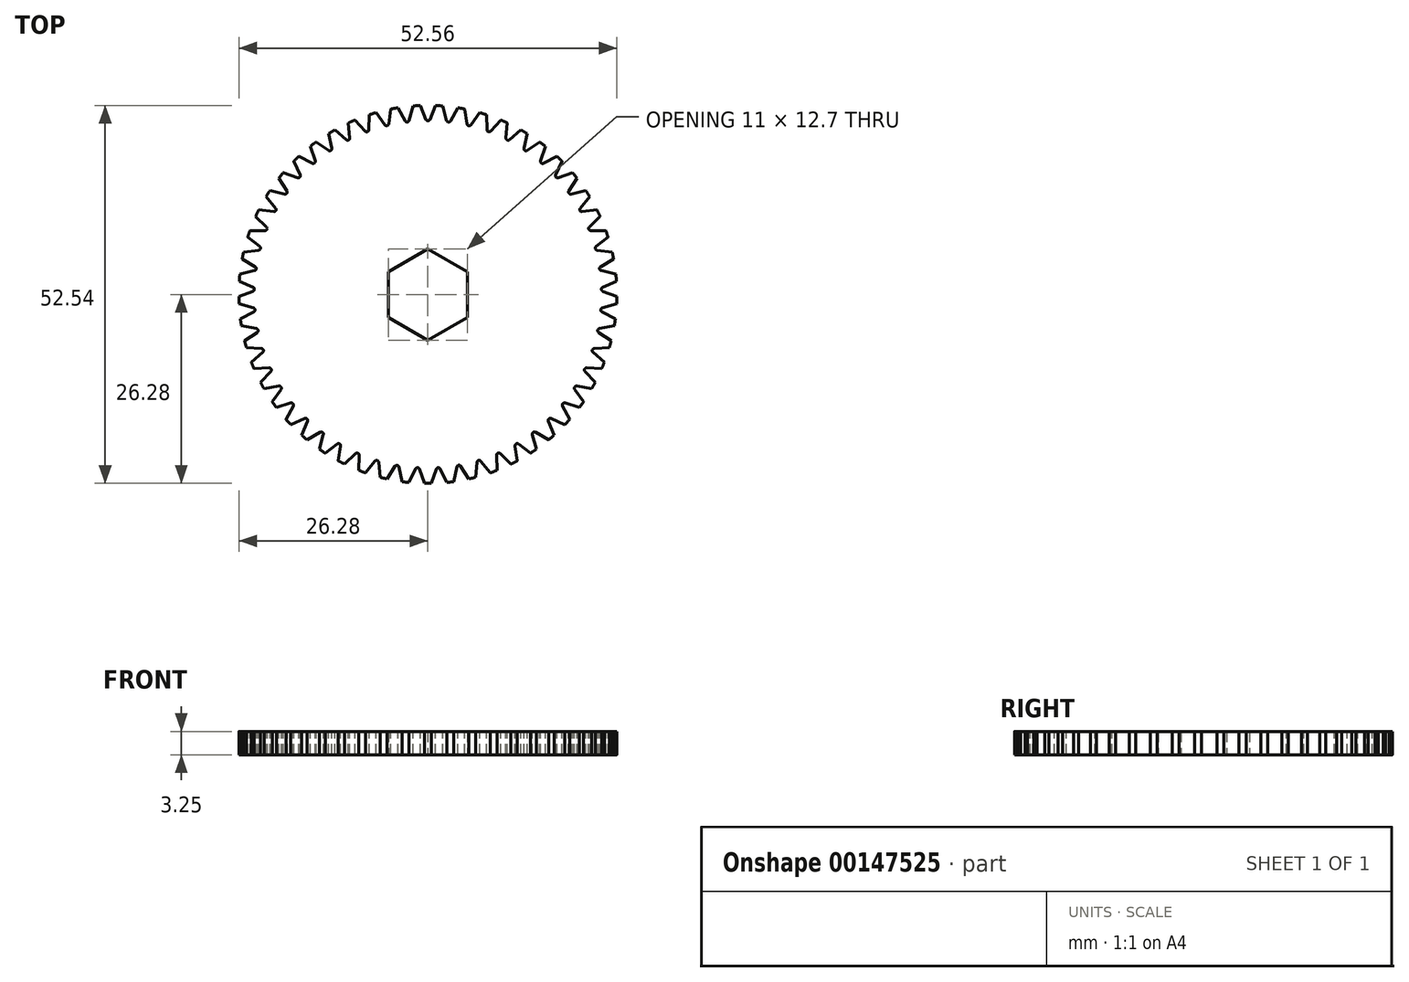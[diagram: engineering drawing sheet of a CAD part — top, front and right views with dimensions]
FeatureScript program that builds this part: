
annotation { "Feature Type Name" : "Feature", "Feature Type Description" : "" }
export const myFeature = defineFeature(function(context is Context, id is Id, definition is map)
    precondition{}
    {
        {
            var Q0;
            Q0=qCreatedBy(makeId("Top.planeOp"),FACE);
            var sketch = newSketch(context, id + "F0", { "sketchPlane" : qUnion([Q0])});
            skCircle(sketch, "E0", {"center": v(0, 0) * mm, "radius": 26.28 * mm});
            skCircle(sketch, "E1.cCircle", {"center": v(0, 0) * mm, "radius": 6.35 * mm, "construction": true});
            skLineSegment(sketch, "E1.0", {"start": v(0, 6.35) * mm, "end": v(5.5, 3.18) * mm});
            skLineSegment(sketch, "E1.1", {"start": v(5.5, 3.18) * mm, "end": v(5.5, -3.17) * mm});
            skLineSegment(sketch, "E1.2", {"start": v(5.5, -3.17) * mm, "end": v(0, -6.35) * mm});
            skLineSegment(sketch, "E1.3", {"start": v(0, -6.35) * mm, "end": v(-5.5, -3.18) * mm});
            skLineSegment(sketch, "E1.4", {"start": v(-5.5, -3.18) * mm, "end": v(-5.5, 3.17) * mm});
            skLineSegment(sketch, "E1.5", {"start": v(-5.5, 3.17) * mm, "end": v(0, 6.35) * mm});
            skSolve(sketch);
        }
        {
            var Q0;
            Q0=qSketchRegion(id+"F0",true);
            extrude(context, id + "F1", {"entities" : qUnion([Q0]), "depth" : 3.25 * mm});
        }
        {
            var Q0;
            Q0=makeQuery(id+"F1.opExtrude","CAP_FACE",FACE,{"disambiguationData":[OSD([sQuery(id+"F0.wireOp",EDGE,"E0")])],"isStart":false});
            var sketch = newSketch(context, id + "F2", { "sketchPlane" : qUnion([Q0])});
            skLineSegment(sketch, "E2", {"start": v(0, 0) * mm, "end": v(0, 26.28) * mm});
            skArc(sketch, "E3", {"start": v(1.06, 26.26) * mm, "mid": v(0, 26.28) * mm, "end": v(-1.06, 26.26) * mm});
            skLineSegment(sketch, "E4", {"start": v(-1.06, 26.26) * mm, "end": v(-0.28, 24.32) * mm});
            skLineSegment(sketch, "E5", {"start": v(1.06, 26.26) * mm, "end": v(0.28, 24.32) * mm});
            skArc(sketch, "E6", {"start": v(-0.28, 24.32) * mm, "mid": v(0, 24.13) * mm, "end": v(0.28, 24.32) * mm});
            skLineSegment(sketch, "E7", {"start": v(0, 0) * mm, "end": v(0.7, 26.27) * mm, "construction": true});
            skPoint(sketch, "E8", {"position": v(0.67, 25.3) * mm});
            skSolve(sketch);
        }
        {
            var Q0;
            Q0=qSketchRegion(id+"F2",true);
            var Q1;
            Q1=makeQuery(id+"F1.opExtrude","CAP_FACE",FACE,{"disambiguationData":[OSD([sQuery(id+"F0.wireOp",EDGE,"E0")])],"isStart":true});
            extrude(context, id + "F3", {"entities" : qUnion([Q0]), "operationType" : NewBodyOperationType.REMOVE, "endBound" : BoundingType.UP_TO_SURFACE, "oppositeDirection" : true, "endBoundEntityFace" : qUnion([Q1]), "depth" : 25.4 * mm});
        }
        {
            var Q0;
            Q0=makeQuery(id+"F3.boolean.opBoolean","COPY",FACE,{"derivedFrom":makeQuery(id+"F3.opExtrude","SWEPT_FACE",FACE,{"disambiguationData":[OSD([sQuery(id+"F2.wireOp",EDGE,"E5")])]})});
            var Q1;
            Q1=makeQuery(id+"F3.boolean.opBoolean","COPY",FACE,{"derivedFrom":makeQuery(id+"F3.opExtrude","SWEPT_FACE",FACE,{"disambiguationData":[OSD([sQuery(id+"F2.wireOp",EDGE,"E6")])]})});
            var Q2;
            Q2=makeQuery(id+"F3.boolean.opBoolean","COPY",FACE,{"derivedFrom":makeQuery(id+"F3.opExtrude","SWEPT_FACE",FACE,{"disambiguationData":[OSD([sQuery(id+"F2.wireOp",EDGE,"E4")])]})});
            var Q3;
            Q3=makeQuery(id+"F1.opExtrude","SWEPT_FACE",FACE,{"disambiguationData":[OSD([sQuery(id+"F0.wireOp",EDGE,"E0")])]});
            circularPattern(context, id + "F4", {"patternType" : PatternType.FACE, "faces" : qUnion([Q0, Q1, Q2]), "axis" : qUnion([Q3]), "angle" : 6.8 * degree, "instanceCount" : 53});
        }
    });
